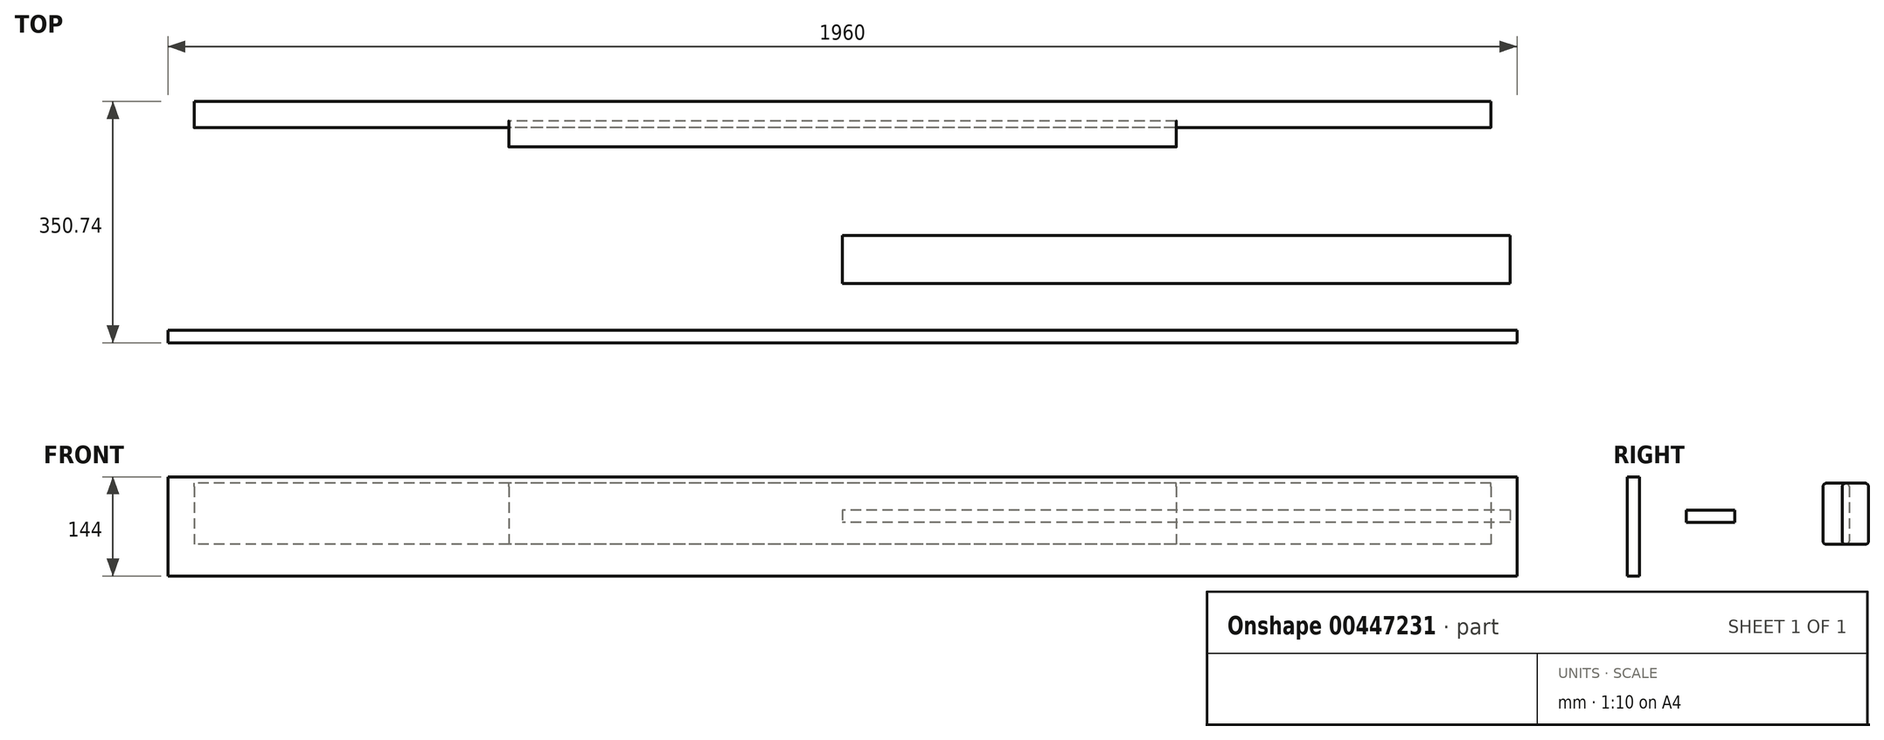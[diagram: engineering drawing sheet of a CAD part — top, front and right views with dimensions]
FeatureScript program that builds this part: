
annotation { "Feature Type Name" : "Feature", "Feature Type Description" : "" }
export const myFeature = defineFeature(function(context is Context, id is Id, definition is map)
    precondition{}
    {
        {
            var Q0;
            Q0=qCreatedBy(makeId("Right.planeOp"),FACE);
            var sketch = newSketch(context, id + "F0", { "sketchPlane" : qUnion([Q0])});
            skLineSegment(sketch, "E0.bottom", {"start": v(11, 44.5) * mm, "end": v(39, 44.5) * mm});
            skLineSegment(sketch, "E0.top", {"start": v(11, -44.5) * mm, "end": v(39, -44.5) * mm});
            skLineSegment(sketch, "E0.left", {"start": v(6, 39.5) * mm, "end": v(6, -39.5) * mm});
            skLineSegment(sketch, "E0.right", {"start": v(44, 39.5) * mm, "end": v(44, -39.5) * mm});
            skPoint(sketch, "E1.visualSharp", {"position": v(6, 44.5) * mm});
            skArc(sketch, "E1.filletArc", {"start": v(11, 44.5) * mm, "mid": v(7.46, 43.04) * mm, "end": v(6, 39.5) * mm});
            skPoint(sketch, "E2.visualSharp", {"position": v(44, 44.5) * mm});
            skArc(sketch, "E2.filletArc", {"start": v(44, 39.5) * mm, "mid": v(42.54, 43.04) * mm, "end": v(39, 44.5) * mm});
            skPoint(sketch, "E3.visualSharp", {"position": v(44, -44.5) * mm});
            skArc(sketch, "E3.filletArc", {"start": v(39, -44.5) * mm, "mid": v(42.54, -43.04) * mm, "end": v(44, -39.5) * mm});
            skPoint(sketch, "E4.visualSharp", {"position": v(6, -44.5) * mm});
            skArc(sketch, "E4.filletArc", {"start": v(6, -39.5) * mm, "mid": v(7.46, -43.04) * mm, "end": v(11, -44.5) * mm});
            skSolve(sketch);
        }
        {
            var Q0;
            Q0=makeQuery(id+"F0.imprint","IMPRINT",FACE,{"disambiguationData":[TD([[makeQuery(id+"F0.imprint","IMPRINT",EDGE,{"derivedFrom":sQuery(id+"F0.wireOp",EDGE,"E0.bottom")}),-1.0]])]});
            extrude(context, id + "F1", {"entities" : qUnion([Q0]), "depth" : 1884 * mm, "symmetric" : true});
        }
        {
            var Q0;
            Q0=qCreatedBy(makeId("Right.planeOp"),FACE);
            var sketch = newSketch(context, id + "F2", { "sketchPlane" : qUnion([Q0])});
            skLineSegment(sketch, "E5.bottom", {"start": v(-306.74, 53.67) * mm, "end": v(-288.74, 53.67) * mm});
            skLineSegment(sketch, "E5.top", {"start": v(-306.74, -90.33) * mm, "end": v(-288.74, -90.33) * mm});
            skLineSegment(sketch, "E5.left", {"start": v(-306.74, 53.67) * mm, "end": v(-306.74, -90.33) * mm});
            skLineSegment(sketch, "E5.right", {"start": v(-288.74, 53.67) * mm, "end": v(-288.74, -90.33) * mm});
            skSolve(sketch);
        }
        {
            var Q0;
            Q0=makeQuery(id+"F2.imprint","IMPRINT",FACE,{"disambiguationData":[TD([[makeQuery(id+"F2.imprint","IMPRINT",EDGE,{"derivedFrom":sQuery(id+"F2.wireOp",EDGE,"E5.bottom")}),-1.0]])]});
            extrude(context, id + "F3", {"entities" : qUnion([Q0]), "depth" : 1960 * mm, "symmetric" : true});
        }
        {
            var Q0;
            Q0=qCreatedBy(makeId("Right.planeOp"),FACE);
            var sketch = newSketch(context, id + "F4", { "sketchPlane" : qUnion([Q0])});
            skLineSegment(sketch, "E6.bottom", {"start": v(-17, 44.5) * mm, "end": v(11, 44.5) * mm});
            skLineSegment(sketch, "E6.top", {"start": v(-17, -44.5) * mm, "end": v(11, -44.5) * mm});
            skLineSegment(sketch, "E6.left", {"start": v(-22, 39.5) * mm, "end": v(-22, -39.5) * mm});
            skLineSegment(sketch, "E6.right", {"start": v(16, 39.5) * mm, "end": v(16, -39.5) * mm});
            skPoint(sketch, "E7.visualSharp", {"position": v(-22, 44.5) * mm});
            skArc(sketch, "E7.filletArc", {"start": v(-17, 44.5) * mm, "mid": v(-20.54, 43.04) * mm, "end": v(-22, 39.5) * mm});
            skPoint(sketch, "E8.visualSharp", {"position": v(16, 44.5) * mm});
            skArc(sketch, "E8.filletArc", {"start": v(16, 39.5) * mm, "mid": v(14.54, 43.04) * mm, "end": v(11, 44.5) * mm});
            skPoint(sketch, "E9.visualSharp", {"position": v(16, -44.5) * mm});
            skArc(sketch, "E9.filletArc", {"start": v(11, -44.5) * mm, "mid": v(14.54, -43.04) * mm, "end": v(16, -39.5) * mm});
            skPoint(sketch, "E10.visualSharp", {"position": v(-22, -44.5) * mm});
            skArc(sketch, "E10.filletArc", {"start": v(-22, -39.5) * mm, "mid": v(-20.54, -43.04) * mm, "end": v(-17, -44.5) * mm});
            skSolve(sketch);
        }
        {
            var Q0;
            Q0=makeQuery(id+"F4.imprint","IMPRINT",FACE,{"disambiguationData":[TD([[makeQuery(id+"F4.imprint","IMPRINT",EDGE,{"derivedFrom":sQuery(id+"F4.wireOp",EDGE,"E6.bottom")}),-1.0]])]});
            extrude(context, id + "F5", {"entities" : qUnion([Q0]), "depth" : 970 * mm, "symmetric" : true});
        }
        {
            var Q0;
            Q0=qCreatedBy(makeId("Right.planeOp"),FACE);
            var sketch = newSketch(context, id + "F6", { "sketchPlane" : qUnion([Q0])});
            skLineSegment(sketch, "E11.bottom", {"start": v(-220.54, 5.44) * mm, "end": v(-150.54, 5.44) * mm});
            skLineSegment(sketch, "E11.top", {"start": v(-220.54, -12.56) * mm, "end": v(-150.54, -12.56) * mm});
            skLineSegment(sketch, "E11.left", {"start": v(-220.54, 5.44) * mm, "end": v(-220.54, -12.56) * mm});
            skLineSegment(sketch, "E11.right", {"start": v(-150.54, 5.44) * mm, "end": v(-150.54, -12.56) * mm});
            skSolve(sketch);
        }
        {
            var Q0;
            Q0=makeQuery(id+"F6.imprint","IMPRINT",FACE,{"disambiguationData":[TD([[makeQuery(id+"F6.imprint","IMPRINT",EDGE,{"derivedFrom":sQuery(id+"F6.wireOp",EDGE,"E11.bottom")}),-1.0]])]});
            extrude(context, id + "F7", {"entities" : qUnion([Q0]), "depth" : 970 * mm});
        }
    });
